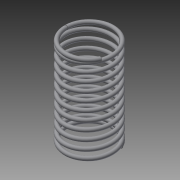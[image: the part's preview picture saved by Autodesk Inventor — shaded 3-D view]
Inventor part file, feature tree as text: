
AUTODESK INVENTOR PART (.ipt)
format: ipt  version: 2014 SP1 (Build 180222100, 222)  size: 706,048 bytes
history: native  units: in
note: dims shown in document units (in); Inventor stores cm internally (conversion verified against a paired STEP export)
features: sketch x3, revolve x2, projected_geometry x2, other x1, helix x1
ambient origin geometry x8: Origin, YZ Plane, XZ Plane, XY Plane, X Axis, Y Axis, Z Axis, Center Point
bodies: Solid1 (feature_tree)
feature tree (9):
  other  "Firing Pin Spring"
  helix  "Coil1"  [1 undecoded]
  revolve  "Revolution1"  [1 undecoded]
  revolve  "Revolution2"  [1 undecoded]
  sketch  "Sketch1"  dims[d2=0.3463in d3=0.3313in]
  sketch  "Sketch2"  dims[d4=1.0in d5=0.3313in]
  projected_geometry  "Projected Loop1"
  sketch  "Sketch3"  dims[d6=3.937in d7=0.0in d8=90.0deg d9=90.0deg d10=90.0deg d11=90.0deg d12=1.0651in d13=1.0651in]
  projected_geometry  "Projected Loop2"
note: 3 required parameter values undecoded (feature->parameter linkage not recoverable at this tier; creation-order binding heuristic only, values carry confidence <= 0.55)